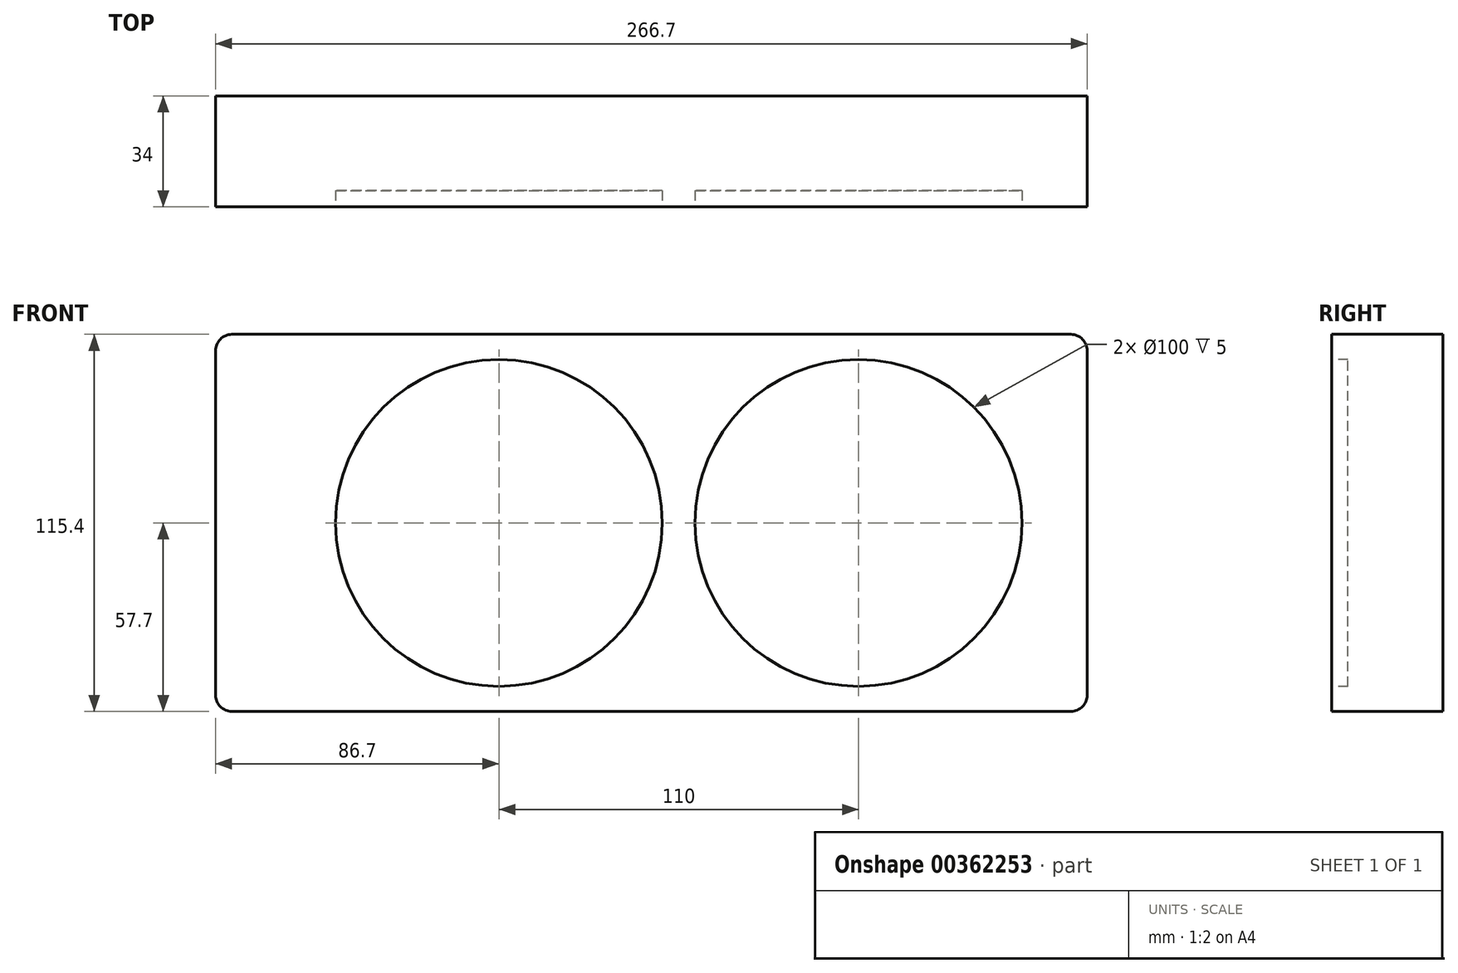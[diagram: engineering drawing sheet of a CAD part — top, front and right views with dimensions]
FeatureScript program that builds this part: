
annotation { "Feature Type Name" : "Feature", "Feature Type Description" : "" }
export const myFeature = defineFeature(function(context is Context, id is Id, definition is map)
    precondition{}
    {
        {
            var Q0;
            Q0=qCreatedBy(makeId("Front.planeOp"),FACE);
            var sketch = newSketch(context, id + "F0", { "sketchPlane" : qUnion([Q0])});
            skLineSegment(sketch, "E0.bottom", {"start": v(5, 0) * mm, "end": v(261.7, 0) * mm});
            skLineSegment(sketch, "E0.top", {"start": v(5, 115.4) * mm, "end": v(261.7, 115.4) * mm});
            skLineSegment(sketch, "E0.left", {"start": v(0, 5) * mm, "end": v(0, 110.4) * mm});
            skLineSegment(sketch, "E0.right", {"start": v(266.7, 5) * mm, "end": v(266.7, 110.4) * mm});
            skPoint(sketch, "E1.visualSharp", {"position": v(0, 115.4) * mm});
            skArc(sketch, "E1.filletArc", {"start": v(5, 115.4) * mm, "mid": v(1.46, 113.94) * mm, "end": v(0, 110.4) * mm});
            skPoint(sketch, "E2.visualSharp", {"position": v(0, 0) * mm});
            skArc(sketch, "E2.filletArc", {"start": v(0, 5) * mm, "mid": v(1.46, 1.46) * mm, "end": v(5, 0) * mm});
            skPoint(sketch, "E3.visualSharp", {"position": v(266.7, 0) * mm});
            skArc(sketch, "E3.filletArc", {"start": v(261.7, 0) * mm, "mid": v(265.24, 1.46) * mm, "end": v(266.7, 5) * mm});
            skPoint(sketch, "E4.visualSharp", {"position": v(266.7, 115.4) * mm});
            skArc(sketch, "E4.filletArc", {"start": v(266.7, 110.4) * mm, "mid": v(265.24, 113.94) * mm, "end": v(261.7, 115.4) * mm});
            skSolve(sketch);
        }
        {
            var Q0;
            Q0=makeQuery(id+"F0.imprint","IMPRINT",FACE,{"disambiguationData":[TD([[makeQuery(id+"F0.imprint","IMPRINT",EDGE,{"derivedFrom":sQuery(id+"F0.wireOp",EDGE,"E0.bottom")}),1.0]])]});
            extrude(context, id + "F1", {"entities" : qUnion([Q0]), "depth" : 34 * mm});
        }
        {
            var Q0;
            Q0=makeQuery(id+"F1.opExtrude","CAP_FACE",FACE,{"disambiguationData":[OSD([sQuery(id+"F0.wireOp",EDGE,"E0.bottom"),sQuery(id+"F0.wireOp",EDGE,"E0.top"),sQuery(id+"F0.wireOp",EDGE,"E0.left"),sQuery(id+"F0.wireOp",EDGE,"E0.right"),sQuery(id+"F0.wireOp",EDGE,"E1.filletArc"),sQuery(id+"F0.wireOp",EDGE,"E2.filletArc"),sQuery(id+"F0.wireOp",EDGE,"E3.filletArc"),sQuery(id+"F0.wireOp",EDGE,"E4.filletArc")])],"isStart":false});
            var sketch = newSketch(context, id + "F2", { "sketchPlane" : qUnion([Q0])});
            skLineSegment(sketch, "E5", {"start": v(0, 57.7) * mm, "end": v(266.7, 57.7) * mm, "construction": true});
            skCircle(sketch, "E6", {"center": v(86.7, 57.7) * mm, "radius": 50 * mm});
            skCircle(sketch, "E7", {"center": v(196.7, 57.7) * mm, "radius": 50 * mm});
            skSolve(sketch);
        }
        {
            var Q0;
            Q0=makeQuery(id+"F2.imprint","IMPRINT",FACE,{"disambiguationData":[TD([[makeQuery(id+"F2.imprint","IMPRINT",EDGE,{"derivedFrom":sQuery(id+"F2.wireOp",EDGE,"E6")}),1.0]])]});
            var Q1;
            Q1=makeQuery(id+"F2.imprint","IMPRINT",FACE,{"disambiguationData":[TD([[makeQuery(id+"F2.imprint","IMPRINT",EDGE,{"derivedFrom":sQuery(id+"F2.wireOp",EDGE,"E7")}),1.0]])]});
            extrude(context, id + "F3", {"entities" : qUnion([Q0, Q1]), "operationType" : NewBodyOperationType.REMOVE, "oppositeDirection" : true, "depth" : 5 * mm});
        }
    });
